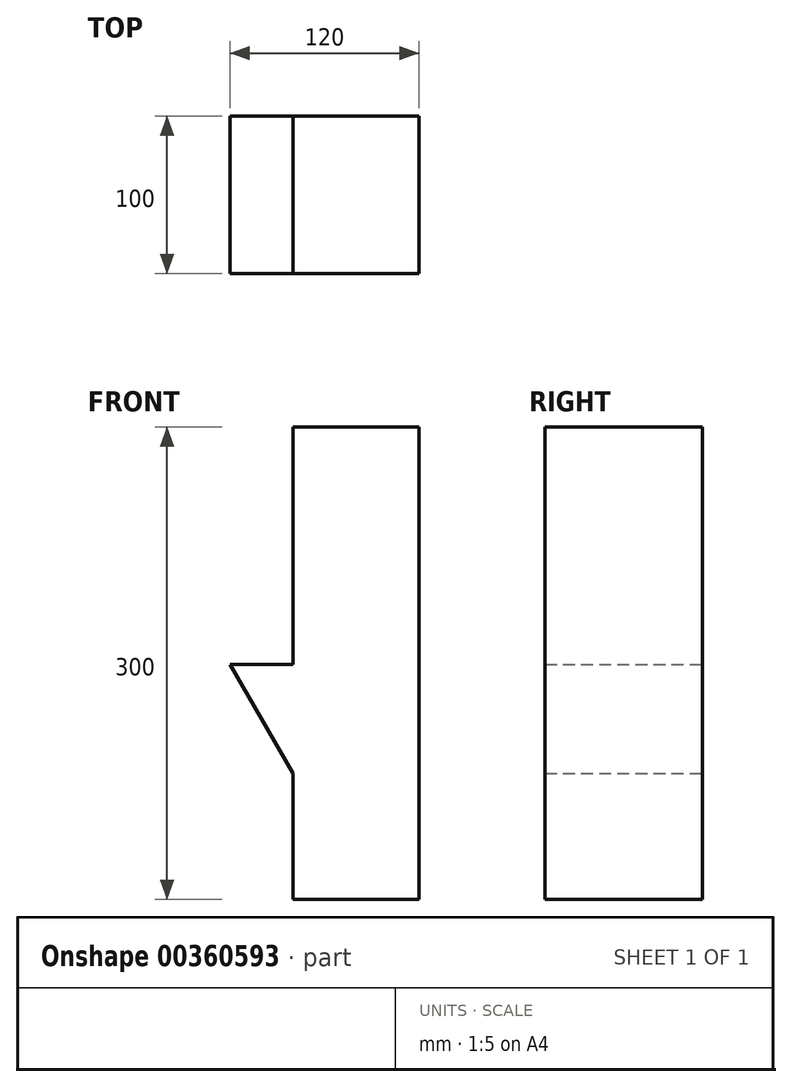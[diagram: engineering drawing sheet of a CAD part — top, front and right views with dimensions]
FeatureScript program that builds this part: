
annotation { "Feature Type Name" : "Feature", "Feature Type Description" : "" }
export const myFeature = defineFeature(function(context is Context, id is Id, definition is map)
    precondition{}
    {
        {
            var Q0;
            Q0=qCreatedBy(makeId("Front.planeOp"),FACE);
            var sketch = newSketch(context, id + "F0", { "sketchPlane" : qUnion([Q0])});
            skLineSegment(sketch, "E0.bottom", {"start": v(40, 150) * mm, "end": v(-40, 150) * mm});
            skLineSegment(sketch, "E0.top", {"start": v(40, -150) * mm, "end": v(-40, -150) * mm});
            skLineSegment(sketch, "E0.left", {"start": v(40, 150) * mm, "end": v(40, -150) * mm});
            skLineSegment(sketch, "E0.right", {"start": v(-40, 150) * mm, "end": v(-40, -150) * mm});
            skPoint(sketch, "E0.middle", {"position": v(0, 0) * mm});
            skLineSegment(sketch, "E1", {"start": v(-40, -0.72) * mm, "end": v(-80, -0.72) * mm});
            skLineSegment(sketch, "E2", {"start": v(-80, -0.72) * mm, "end": v(-40, -70) * mm});
            skSolve(sketch);
        }
        {
            var Q0;
            {var subQ1=sQuery(id+"F0.wireOp",EDGE,"E0.bottom");Q0=makeQuery(id+"F0.imprint","IMPRINT",FACE,{"disambiguationData":[TD([[makeQuery(id+"F0.imprint","IMPRINT",EDGE,{"derivedFrom":subQ1}),1.0]])]});}
            var Q1;
            {var subQ0=sQuery(id+"F0.wireOp",EDGE,"E1");Q1=makeQuery(id+"F0.imprint","IMPRINT",FACE,{"disambiguationData":[TD([[makeQuery(id+"F0.imprint","IMPRINT",EDGE,{"derivedFrom":subQ0}),1.0]])]});}
            extrude(context, id + "F1", {"entities" : qUnion([Q0, Q1]), "depth" : 100 * mm});
        }
    });
